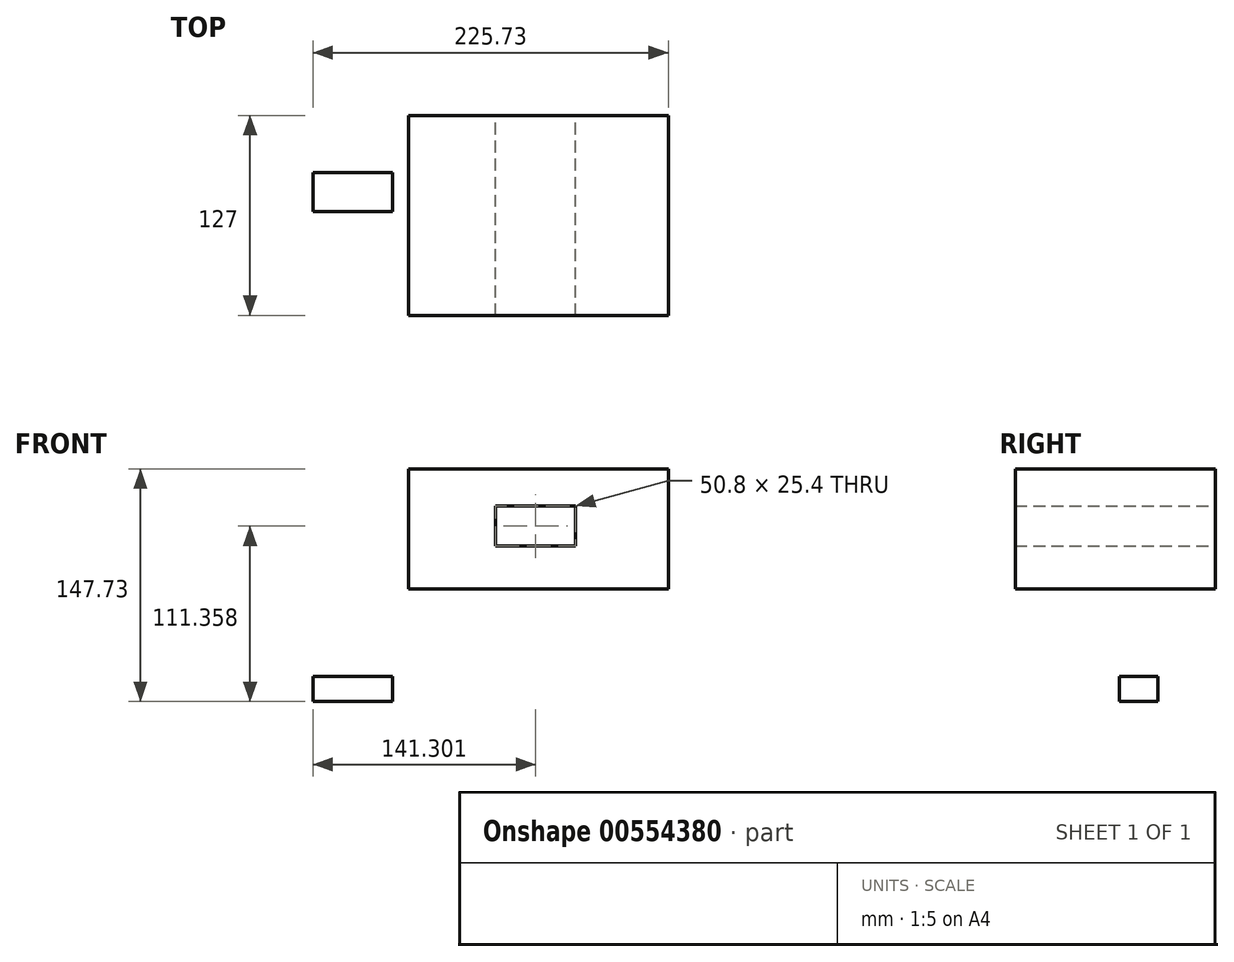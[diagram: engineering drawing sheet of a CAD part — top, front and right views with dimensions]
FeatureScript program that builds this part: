
annotation { "Feature Type Name" : "Feature", "Feature Type Description" : "" }
export const myFeature = defineFeature(function(context is Context, id is Id, definition is map)
    precondition{}
    {
        {
            var Q0;
            Q0=qCreatedBy(makeId("Front.planeOp"),FACE);
            var sketch = newSketch(context, id + "F0", { "sketchPlane" : qUnion([Q0])});
            skLineSegment(sketch, "E0.bottom", {"start": v(-271.82, 20.71) * mm, "end": v(103.27, 20.71) * mm});
            skLineSegment(sketch, "E0.top", {"start": v(-271.82, -73.23) * mm, "end": v(103.27, -73.23) * mm});
            skLineSegment(sketch, "E0.left", {"start": v(-271.82, 20.71) * mm, "end": v(-271.82, -73.23) * mm});
            skLineSegment(sketch, "E0.right", {"start": v(103.27, 20.71) * mm, "end": v(103.27, -73.23) * mm});
            skLineSegment(sketch, "E1.bottom", {"start": v(-224.35, 96.91) * mm, "end": v(-59.19, 96.91) * mm});
            skLineSegment(sketch, "E1.top", {"start": v(-224.35, 20.71) * mm, "end": v(-59.19, 20.71) * mm});
            skLineSegment(sketch, "E1.left", {"start": v(-224.35, 96.91) * mm, "end": v(-224.35, 20.71) * mm});
            skLineSegment(sketch, "E1.right", {"start": v(-59.19, 96.91) * mm, "end": v(-59.19, 20.71) * mm});
            skLineSegment(sketch, "E2.top", {"start": v(-197.74, 20.71) * mm, "end": v(-83.96, 20.71) * mm});
            skLineSegment(sketch, "E3.bottom", {"start": v(-169.02, 73.24) * mm, "end": v(-118.22, 73.24) * mm});
            skLineSegment(sketch, "E3.top", {"start": v(-169.02, 47.84) * mm, "end": v(-118.22, 47.84) * mm});
            skLineSegment(sketch, "E3.left", {"start": v(-169.02, 73.24) * mm, "end": v(-169.02, 47.84) * mm});
            skLineSegment(sketch, "E3.right", {"start": v(-118.22, 73.24) * mm, "end": v(-118.22, 47.84) * mm});
            skPoint(sketch, "E4.oppositeSnap0", {"position": v(-248.38, -50.82) * mm});
            skLineSegment(sketch, "E4.bottom", {"start": v(-284.92, -34.88) * mm, "end": v(-234.45, -34.88) * mm});
            skLineSegment(sketch, "E4.top", {"start": v(-284.92, -50.82) * mm, "end": v(-234.45, -50.82) * mm});
            skLineSegment(sketch, "E4.left", {"start": v(-284.92, -34.88) * mm, "end": v(-284.92, -50.82) * mm});
            skLineSegment(sketch, "E4.right", {"start": v(-234.45, -34.88) * mm, "end": v(-234.45, -50.82) * mm});
            skLineSegment(sketch, "E5.bottom", {"start": v(-160.12, 96.91) * mm, "end": v(-161.96, 96.91) * mm});
            skLineSegment(sketch, "E5.top", {"start": v(-160.12, 122.03) * mm, "end": v(-161.96, 122.03) * mm});
            skLineSegment(sketch, "E6", {"start": v(-328.57, -63.94) * mm, "end": v(-284.92, -17.44) * mm});
            skLineSegment(sketch, "E7", {"start": v(-293.17, -64.24) * mm, "end": v(-324.37, -10.1) * mm});
            skLineSegment(sketch, "E8", {"start": v(-339.97, -42.22) * mm, "end": v(-284.92, -40.7) * mm});
            skPoint(sketch, "E8.endSnap0", {"position": v(-306.74, -40.7) * mm});
            skArc(sketch, "E9", {"start": v(-271.82, 0) * mm, "mid": v(-84.28, -80.89) * mm, "end": v(103.27, 0) * mm});
            skSolve(sketch);
        }
        {
            var Q0;
            {var subQ0=sQuery(id+"F0.wireOp",EDGE,"E7");var subQ1=sQuery(id+"F0.wireOp",EDGE,"E6");var subQ2=makeQuery(id+"F0.imprint","INTERSECT",VERTEX,{"derivedFrom":[subQ1,subQ0]});Q0=makeQuery(id+"F0.imprint","IMPRINT",FACE,{"disambiguationData":[TD([[makeQuery(id+"F0.imprint","IMPRINT",EDGE,{"disambiguationData":[TD([[subQ2,1.0]])],"derivedFrom":subQ1}),-1.0]])]});}
            var Q1;
            {var subQ0=sQuery(id+"F0.wireOp",EDGE,"E9");var subQ1=sQuery(id+"F0.wireOp",EDGE,"E0.top");var subQ2=makeQuery(id+"F0.imprint","INTERSECT",VERTEX,{"disambiguationData":[OD(0.0)],"derivedFrom":[subQ1,subQ0]});Q1=makeQuery(id+"F0.imprint","IMPRINT",FACE,{"disambiguationData":[TD([[makeQuery(id+"F0.imprint","IMPRINT",EDGE,{"disambiguationData":[TD([[subQ2,-1.0]])],"derivedFrom":subQ1}),-1.0]])]});}
            var Q2;
            {var subQ2=sQuery(id+"F0.wireOp",EDGE,"E1.left");Q2=makeQuery(id+"F0.imprint","IMPRINT",FACE,{"disambiguationData":[TD([[makeQuery(id+"F0.imprint","IMPRINT",EDGE,{"derivedFrom":subQ2}),1.0]])]});}
            var Q3;
            {var subQ7=sQuery(id+"F0.wireOp",EDGE,"E2.top");Q3=makeQuery(id+"F0.imprint","IMPRINT",FACE,{"disambiguationData":[TD([[makeQuery(id+"F0.imprint","IMPRINT",EDGE,{"derivedFrom":subQ7}),-1.0]])]});}
            var Q4;
            Q4=makeQuery(id+"F0.imprint","IMPRINT",FACE,{"disambiguationData":[TD([[makeQuery(id+"F0.imprint","IMPRINT",EDGE,{"derivedFrom":sQuery(id+"F0.wireOp",EDGE,"a3acd2e9-cc9e-4f02-85ef-6333b1a207a8.sketch_text.stroke-55")}),1.0]])]});
            extrude(context, id + "F1", {"entities" : qUnion([Q0, Q1, Q2, Q3, Q4]), "depth" : 127 * mm, "offsetDistance" : 25.4 * mm});
        }
        {
            var Q0;
            {var subQ0=sQuery(id+"F0.wireOp",EDGE,"E4.left");var subQ3=makeQuery(id+"F0.imprint","IMPRINT",VERTEX,{"derivedFrom":subQ0});Q0=makeQuery(id+"F0.imprint","IMPRINT",FACE,{"disambiguationData":[TD([[makeQuery(id+"F0.imprint","IMPRINT",EDGE,{"disambiguationData":[TD([[subQ3,1.0]])],"derivedFrom":subQ0}),1.0]])]});}
            var Q1;
            {var subQ5=sQuery(id+"F0.wireOp",EDGE,"E4.right");Q1=makeQuery(id+"F0.imprint","IMPRINT",FACE,{"disambiguationData":[TD([[makeQuery(id+"F0.imprint","IMPRINT",EDGE,{"derivedFrom":subQ5}),-1.0]])]});}
            extrude(context, id + "F2", {"entities" : qUnion([Q0, Q1]), "depth" : 60.96 * mm, "offsetDistance" : 25.4 * mm, "hasSecondDirection" : true, "secondDirectionOppositeDirection" : false, "secondDirectionDepth" : 36.32 * mm});
        }
        {
            var Q0;
            Q0=makeQuery(id+"F1.opExtrude","SWEPT_BODY",BODY,{"disambiguationData":[OSD([sQuery(id+"F0.wireOp",EDGE,"E6"),sQuery(id+"F0.wireOp",EDGE,"E7"),sQuery(id+"F0.wireOp",EDGE,"E8")])]});
            deleteBodies(context, id + "F3", {"entities" : qUnion([Q0])});
        }
    });
